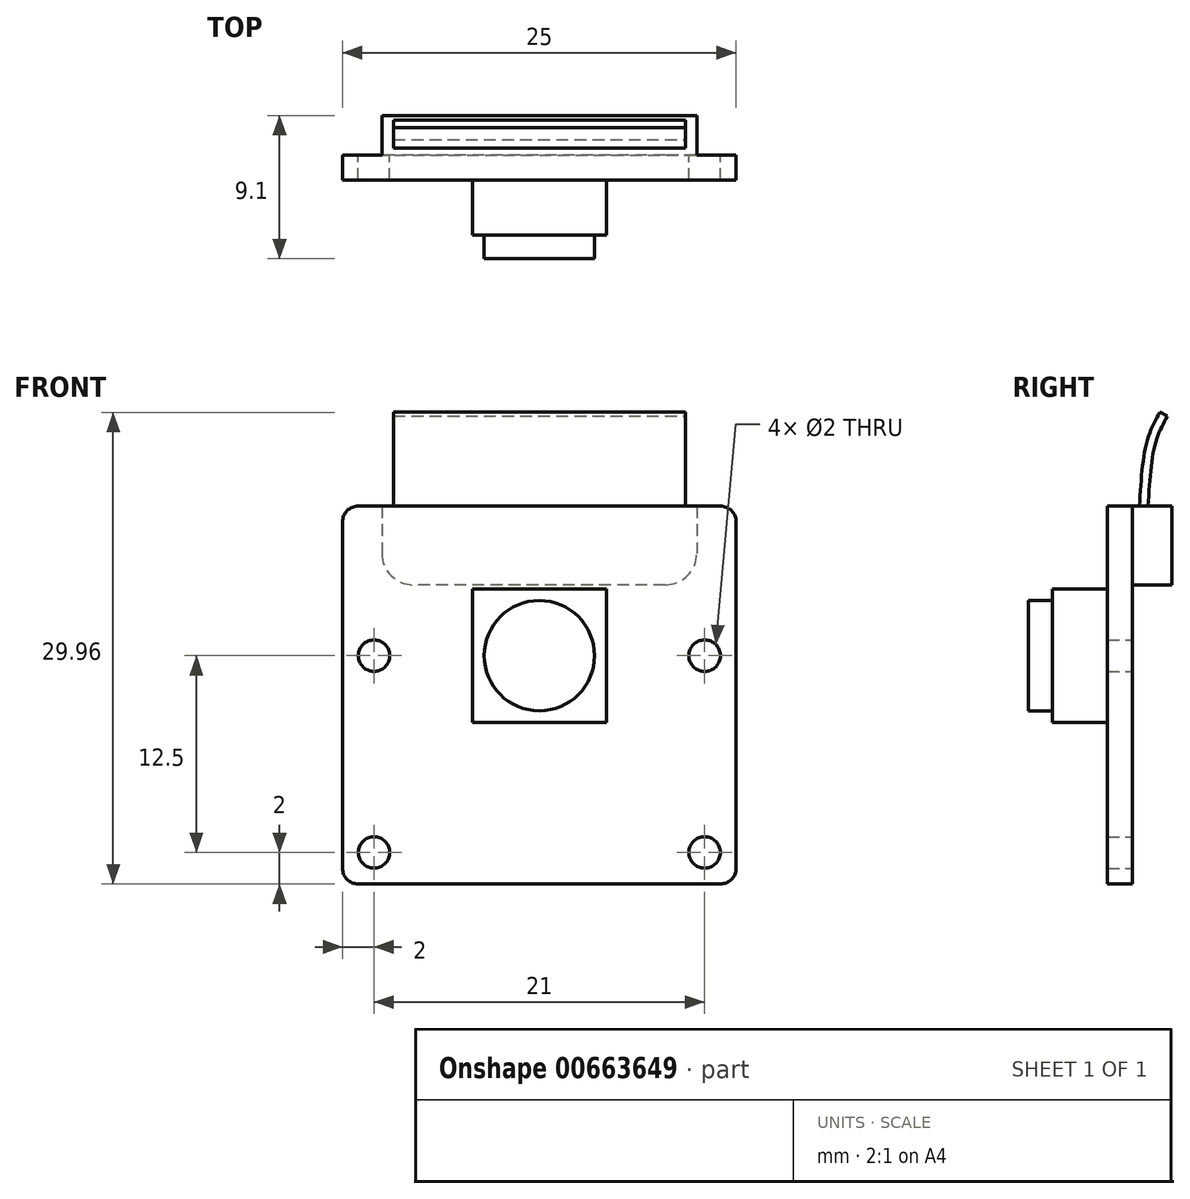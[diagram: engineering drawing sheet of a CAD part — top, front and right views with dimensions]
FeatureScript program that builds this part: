
annotation { "Feature Type Name" : "Feature", "Feature Type Description" : "" }
export const myFeature = defineFeature(function(context is Context, id is Id, definition is map)
    precondition{}
    {
        {
            var Q0;
            Q0=qCreatedBy(makeId("Front.planeOp"),FACE);
            var sketch = newSketch(context, id + "F0", { "sketchPlane" : qUnion([Q0])});
            skLineSegment(sketch, "E0.bottom", {"start": v(-11.5, 12) * mm, "end": v(11.5, 12) * mm});
            skLineSegment(sketch, "E0.top", {"start": v(-11.5, -12) * mm, "end": v(11.5, -12) * mm});
            skLineSegment(sketch, "E0.left", {"start": v(-12.5, 11) * mm, "end": v(-12.5, -11) * mm});
            skLineSegment(sketch, "E0.right", {"start": v(12.5, 11) * mm, "end": v(12.5, -11) * mm});
            skPoint(sketch, "E0.middle", {"position": v(0, 0) * mm});
            skPoint(sketch, "E1.visualSharp", {"position": v(-12.5, 12) * mm});
            skArc(sketch, "E1.filletArc", {"start": v(-11.5, 12) * mm, "mid": v(-12.2, 11.7) * mm, "end": v(-12.5, 11) * mm});
            skPoint(sketch, "E2.visualSharp", {"position": v(12.5, 12) * mm});
            skArc(sketch, "E2.filletArc", {"start": v(12.5, 11) * mm, "mid": v(12.2, 11.7) * mm, "end": v(11.5, 12) * mm});
            skPoint(sketch, "E3.visualSharp", {"position": v(12.5, -12) * mm});
            skArc(sketch, "E3.filletArc", {"start": v(11.5, -12) * mm, "mid": v(12.2, -11.7) * mm, "end": v(12.5, -11) * mm});
            skPoint(sketch, "E4.visualSharp", {"position": v(-12.5, -12) * mm});
            skArc(sketch, "E4.filletArc", {"start": v(-12.5, -11) * mm, "mid": v(-12.2, -11.7) * mm, "end": v(-11.5, -12) * mm});
            skCircle(sketch, "E5", {"center": v(-10.5, -10) * mm, "radius": 1 * mm});
            skCircle(sketch, "E6", {"center": v(-10.5, 2.5) * mm, "radius": 1 * mm});
            skLineSegment(sketch, "E7", {"start": v(0, 12) * mm, "end": v(0, -12) * mm, "construction": true});
            skCircle(sketch, "E8.MirrorC", {"center": v(10.5, 2.5) * mm, "radius": 1 * mm});
            skCircle(sketch, "E9.MirrorC", {"center": v(10.5, -10) * mm, "radius": 1 * mm});
            skSolve(sketch);
        }
        {
            var Q0;
            Q0 = qSketchRegion(id + "F0", true);
            extrude(context, id + "F1", {"entities" : qUnion([Q0]), "depth" : 1.6 * mm, "offsetDistance" : 25 * mm});
        }
        {
            var Q0;
            Q0=makeQuery(id+"F1.opExtrude","CAP_FACE",FACE,{"disambiguationData":[OSD([sQuery(id+"F0.wireOp",EDGE,"E0.bottom"),sQuery(id+"F0.wireOp",EDGE,"E0.top"),sQuery(id+"F0.wireOp",EDGE,"E0.left"),sQuery(id+"F0.wireOp",EDGE,"E0.right"),sQuery(id+"F0.wireOp",EDGE,"E1.filletArc"),sQuery(id+"F0.wireOp",EDGE,"E2.filletArc"),sQuery(id+"F0.wireOp",EDGE,"E3.filletArc"),sQuery(id+"F0.wireOp",EDGE,"E4.filletArc"),sQuery(id+"F0.wireOp",EDGE,"E5"),sQuery(id+"F0.wireOp",EDGE,"E6"),sQuery(id+"F0.wireOp",EDGE,"E8.MirrorC"),sQuery(id+"F0.wireOp",EDGE,"E9.MirrorC")])],"isStart":true});
            var sketch = newSketch(context, id + "F2", { "sketchPlane" : qUnion([Q0])});
            skLineSegment(sketch, "E10.bottom", {"start": v(-10, 12) * mm, "end": v(10, 12) * mm});
            skLineSegment(sketch, "E10.top", {"start": v(-8, 7) * mm, "end": v(8, 7) * mm});
            skLineSegment(sketch, "E10.left", {"start": v(-10, 12) * mm, "end": v(-10, 9) * mm});
            skLineSegment(sketch, "E10.right", {"start": v(10, 12) * mm, "end": v(10, 9) * mm});
            skPoint(sketch, "E11.visualSharp", {"position": v(-10, 7) * mm});
            skArc(sketch, "E11.filletArc", {"start": v(-10, 9) * mm, "mid": v(-9.41, 7.59) * mm, "end": v(-8, 7) * mm});
            skPoint(sketch, "E12.visualSharp", {"position": v(10, 7) * mm});
            skArc(sketch, "E12.filletArc", {"start": v(8, 7) * mm, "mid": v(9.41, 7.59) * mm, "end": v(10, 9) * mm});
            skSolve(sketch);
        }
        {
            var Q0;
            Q0 = qSketchRegion(id + "F2", true);
            extrude(context, id + "F3", {"entities" : qUnion([Q0]), "operationType" : NewBodyOperationType.ADD, "depth" : 2.5 * mm, "offsetDistance" : 25 * mm});
        }
        {
            var Q0;
            Q0=makeQuery(id+"F3.boolean.opBoolean","MERGE",FACE,{"derivedFrom":[makeQuery(id+"F1.opExtrude","SWEPT_FACE",FACE,{"disambiguationData":[OSD([sQuery(id+"F0.wireOp",EDGE,"E0.bottom")])]}),makeQuery(id+"F3.opExtrude","SWEPT_FACE",FACE,{"disambiguationData":[OSD([sQuery(id+"F2.wireOp",EDGE,"E10.bottom")])]})]});
            var sketch = newSketch(context, id + "F4", { "sketchPlane" : qUnion([Q0])});
            skLineSegment(sketch, "E13.bottom", {"start": v(-9.27, 0.98) * mm, "end": v(9.27, 0.98) * mm});
            skLineSegment(sketch, "E13.top", {"start": v(-9.27, 0.43) * mm, "end": v(9.27, 0.43) * mm});
            skLineSegment(sketch, "E13.left", {"start": v(-9.27, 0.98) * mm, "end": v(-9.27, 0.43) * mm});
            skLineSegment(sketch, "E13.right", {"start": v(9.27, 0.98) * mm, "end": v(9.27, 0.43) * mm});
            skPoint(sketch, "E13.middle", {"position": v(0, 0.7) * mm});
            skSolve(sketch);
        }
        {
            var Q0;
            Q0=qCreatedBy(makeId("Right.planeOp"),FACE);
            var sketch = newSketch(context, id + "F5", { "sketchPlane" : qUnion([Q0])});
            skFitSpline(sketch, "E14", {"points": [v(0.68, 12.04) * mm, v(1.15, 16.06) * mm, v(1.97, 17.9) * mm], "startDerivative": vector(0.46, 7.55) * mm, "endDerivative": vector(2.23, 3.94) * mm});
            skSolve(sketch);
        }
        {
            var Q0;
            Q0 = qSketchRegion(id + "F4", true);
            var Q1;
            Q1 = qConstructionFilter(qBodyType(qCreatedBy(id + "F5" ,EDGE), BodyType.WIRE), ConstructionObject.NO);
            sweep(context, id + "F6", {"operationType" : NewBodyOperationType.ADD, "profiles" : qUnion([Q0]), "path" : qUnion([Q1])});
        }
        {
            var Q0;
            Q0=makeQuery(id+"F1.opExtrude","CAP_FACE",FACE,{"disambiguationData":[OSD([sQuery(id+"F0.wireOp",EDGE,"E0.bottom"),sQuery(id+"F0.wireOp",EDGE,"E0.top"),sQuery(id+"F0.wireOp",EDGE,"E0.left"),sQuery(id+"F0.wireOp",EDGE,"E0.right"),sQuery(id+"F0.wireOp",EDGE,"E1.filletArc"),sQuery(id+"F0.wireOp",EDGE,"E2.filletArc"),sQuery(id+"F0.wireOp",EDGE,"E3.filletArc"),sQuery(id+"F0.wireOp",EDGE,"E4.filletArc"),sQuery(id+"F0.wireOp",EDGE,"E5"),sQuery(id+"F0.wireOp",EDGE,"E6"),sQuery(id+"F0.wireOp",EDGE,"E8.MirrorC"),sQuery(id+"F0.wireOp",EDGE,"E9.MirrorC")])],"isStart":false});
            var sketch = newSketch(context, id + "F7", { "sketchPlane" : qUnion([Q0])});
            skLineSegment(sketch, "E15", {"start": v(-10.5, 2.5) * mm, "end": v(10.5, 2.5) * mm, "construction": true});
            skCircle(sketch, "E16", {"center": v(0, 2.5) * mm, "radius": 3.5 * mm});
            skLineSegment(sketch, "E17.bottom", {"start": v(4.25, -1.75) * mm, "end": v(-4.25, -1.75) * mm});
            skLineSegment(sketch, "E17.top", {"start": v(4.25, 6.75) * mm, "end": v(-4.25, 6.75) * mm});
            skLineSegment(sketch, "E17.left", {"start": v(4.25, -1.75) * mm, "end": v(4.25, 6.75) * mm});
            skLineSegment(sketch, "E17.right", {"start": v(-4.25, -1.75) * mm, "end": v(-4.25, 6.75) * mm});
            skSolve(sketch);
        }
        {
            var Q0;
            Q0=makeQuery(id+"F7.imprint","IMPRINT",FACE,{"disambiguationData":[TD([[makeQuery(id+"F7.imprint","IMPRINT",EDGE,{"derivedFrom":sQuery(id+"F7.wireOp",EDGE,"E16")}),1.0]])]});
            extrude(context, id + "F8", {"entities" : qUnion([Q0]), "operationType" : NewBodyOperationType.ADD, "depth" : 5 * mm, "offsetDistance" : 25 * mm});
        }
        {
            var Q0;
            Q0=makeQuery(id+"F7.imprint","IMPRINT",FACE,{"disambiguationData":[TD([[makeQuery(id+"F7.imprint","IMPRINT",EDGE,{"derivedFrom":sQuery(id+"F7.wireOp",EDGE,"E16")}),-1.0]])]});
            extrude(context, id + "F9", {"entities" : qUnion([Q0]), "operationType" : NewBodyOperationType.ADD, "depth" : 3.5 * mm, "offsetDistance" : 25 * mm});
        }
    });
